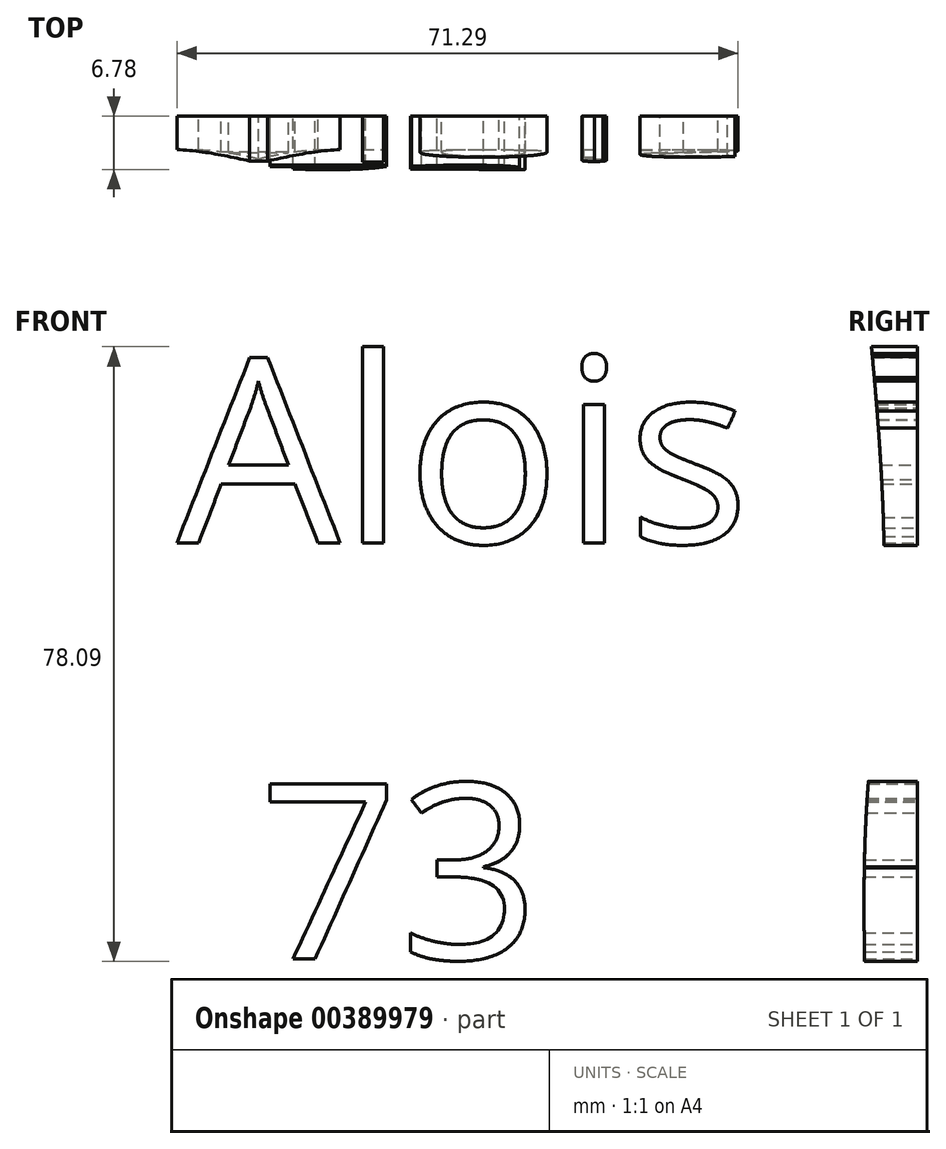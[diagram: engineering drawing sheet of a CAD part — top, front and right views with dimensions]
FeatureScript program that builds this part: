
annotation { "Feature Type Name" : "Feature", "Feature Type Description" : "" }
export const myFeature = defineFeature(function(context is Context, id is Id, definition is map)
    precondition{}
    {
        {
            var Q0;
            Q0=qCreatedBy(makeId("Front.planeOp"),FACE);
            var sketch = newSketch(context, id + "F0", { "sketchPlane" : qUnion([Q0])});
            skText(sketch, "E0", { "text": "Alois", "fontName": "OpenSans-Regular.ttf"});
            skText(sketch, "E1", { "text": "73", "fontName": "OpenSans-Regular.ttf"});
            const initialGuessF0  = {"E0": [-0.06405, 0.02462, 1, 0, 0.02361], "E1": [-0.05362, -0.02824, 1, 0, 0.02243]};
            skSetInitialGuess(sketch, initialGuessF0);
            skSolve(sketch);
        }
        {
            var Q0;
            Q0=qCreatedBy(makeId("Right.planeOp"),FACE);
            var sketch = newSketch(context, id + "F1", { "sketchPlane" : qUnion([Q0])});
            skFitSpline(sketch, "E2", {"points": [v(-3.94, -81.81) * mm, v(-6.57, -11.4) * mm, v(-4.24, 20.16) * mm, v(-9.79, 84.73) * mm], "startDerivative": vector(-13.5, 207.7) * mm, "endDerivative": vector(-23.7, 197.14) * mm});
            skSolve(sketch);
        }
        {
            var Q0;
            Q0=sQuery(id+"F1.wireOp",EDGE,"E2");
            extrude(context, id + "F2", {"bodyType" : ToolBodyType.SURFACE, "surfaceEntities" : qUnion([Q0]), "depth" : 99.3 * mm, "hasSecondDirection" : true, "secondDirectionOppositeDirection" : true, "secondDirectionDepth" : 118.2 * mm});
        }
        {
            var Q0;
            Q0 = qSketchRegion(id + "F0", true);
            var Q1;
            Q1=makeQuery(id+"F2.opExtrude","SWEPT_FACE",FACE,{"disambiguationData":[OSD([sQuery(id+"F1.wireOp",EDGE,"E2")])]});
            extrude(context, id + "F3", {"entities" : qUnion([Q0]), "endBound" : BoundingType.UP_TO_SURFACE, "endBoundEntityFace" : qUnion([Q1]), "depth" : 10 * mm});
        }
    });
